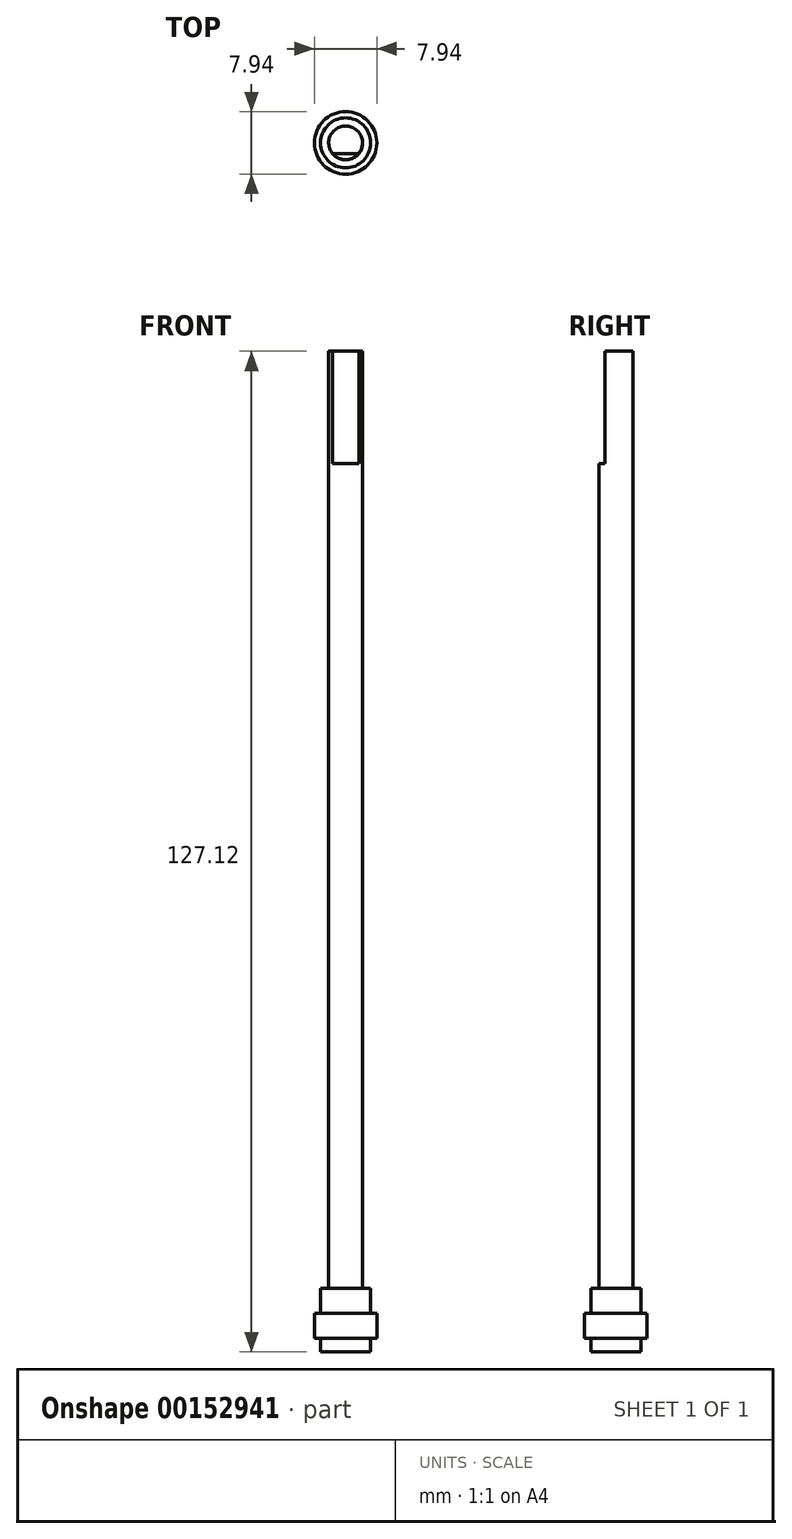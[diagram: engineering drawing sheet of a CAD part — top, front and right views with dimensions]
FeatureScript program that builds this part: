
annotation { "Feature Type Name" : "Feature", "Feature Type Description" : "" }
export const myFeature = defineFeature(function(context is Context, id is Id, definition is map)
    precondition{}
    {
        {
            var Q0;
            Q0=qCreatedBy(makeId("Top.planeOp"),FACE);
            var sketch = newSketch(context, id + "F0", { "sketchPlane" : qUnion([Q0])});
            skCircle(sketch, "E0", {"center": v(0, 0) * mm, "radius": 3.18 * mm});
            skSolve(sketch);
        }
        {
            var Q0;
            Q0 = qSketchRegion(id + "F0", true);
            extrude(context, id + "F1", {"entities" : qUnion([Q0]), "depth" : 1.7 * mm});
        }
        {
            var Q0;
            Q0=makeQuery(id+"F1.opExtrude","CAP_FACE",FACE,{"disambiguationData":[OSD([sQuery(id+"F0.wireOp",EDGE,"E0")])],"isStart":false});
            var sketch = newSketch(context, id + "F2", { "sketchPlane" : qUnion([Q0])});
            skCircle(sketch, "E1", {"center": v(0, 0) * mm, "radius": 3.97 * mm});
            skSolve(sketch);
        }
        {
            var Q0;
            Q0 = qSketchRegion(id + "F2", true);
            extrude(context, id + "F3", {"entities" : qUnion([Q0]), "operationType" : NewBodyOperationType.ADD, "depth" : 3.17 * mm});
        }
        {
            var Q0;
            Q0=makeQuery(id+"F3.opExtrude","CAP_FACE",FACE,{"disambiguationData":[OSD([sQuery(id+"F2.wireOp",EDGE,"E1")])],"isStart":false});
            var sketch = newSketch(context, id + "F4", { "sketchPlane" : qUnion([Q0])});
            skCircle(sketch, "E2", {"center": v(0, 0) * mm, "radius": 3.18 * mm});
            skSolve(sketch);
        }
        {
            var Q0;
            Q0 = qSketchRegion(id + "F4", true);
            extrude(context, id + "F5", {"entities" : qUnion([Q0]), "operationType" : NewBodyOperationType.ADD, "depth" : 3.17 * mm});
        }
        {
            var Q0;
            Q0=makeQuery(id+"F5.opExtrude","CAP_FACE",FACE,{"disambiguationData":[OSD([sQuery(id+"F4.wireOp",EDGE,"E2")])],"isStart":false});
            var sketch = newSketch(context, id + "F6", { "sketchPlane" : qUnion([Q0])});
            skCircle(sketch, "E3", {"center": v(0, 0) * mm, "radius": 2.15 * mm});
            skSolve(sketch);
        }
        {
            var Q0;
            Q0 = qSketchRegion(id + "F6", true);
            extrude(context, id + "F7", {"entities" : qUnion([Q0]), "operationType" : NewBodyOperationType.ADD, "depth" : 119.06 * mm});
        }
        {
            var Q0;
            Q0=makeQuery(id+"F7.opExtrude","CAP_FACE",FACE,{"disambiguationData":[OSD([sQuery(id+"F6.wireOp",EDGE,"E3")])],"isStart":false});
            var sketch = newSketch(context, id + "F8", { "sketchPlane" : qUnion([Q0])});
            skLineSegment(sketch, "E4.bottom", {"start": v(1.67, -1.36) * mm, "end": v(-1.67, -1.36) * mm});
            skLineSegment(sketch, "E4.top", {"start": v(1.67, -2.15) * mm, "end": v(-1.67, -2.15) * mm});
            skLineSegment(sketch, "E4.left", {"start": v(1.67, -1.36) * mm, "end": v(1.67, -2.15) * mm});
            skLineSegment(sketch, "E4.right", {"start": v(-1.67, -1.36) * mm, "end": v(-1.67, -2.15) * mm});
            skSolve(sketch);
        }
        {
            var Q0;
            Q0 = qSketchRegion(id + "F8", true);
            extrude(context, id + "F9", {"entities" : qUnion([Q0]), "operationType" : NewBodyOperationType.REMOVE, "oppositeDirection" : true, "depth" : 14.29 * mm});
        }
    });
